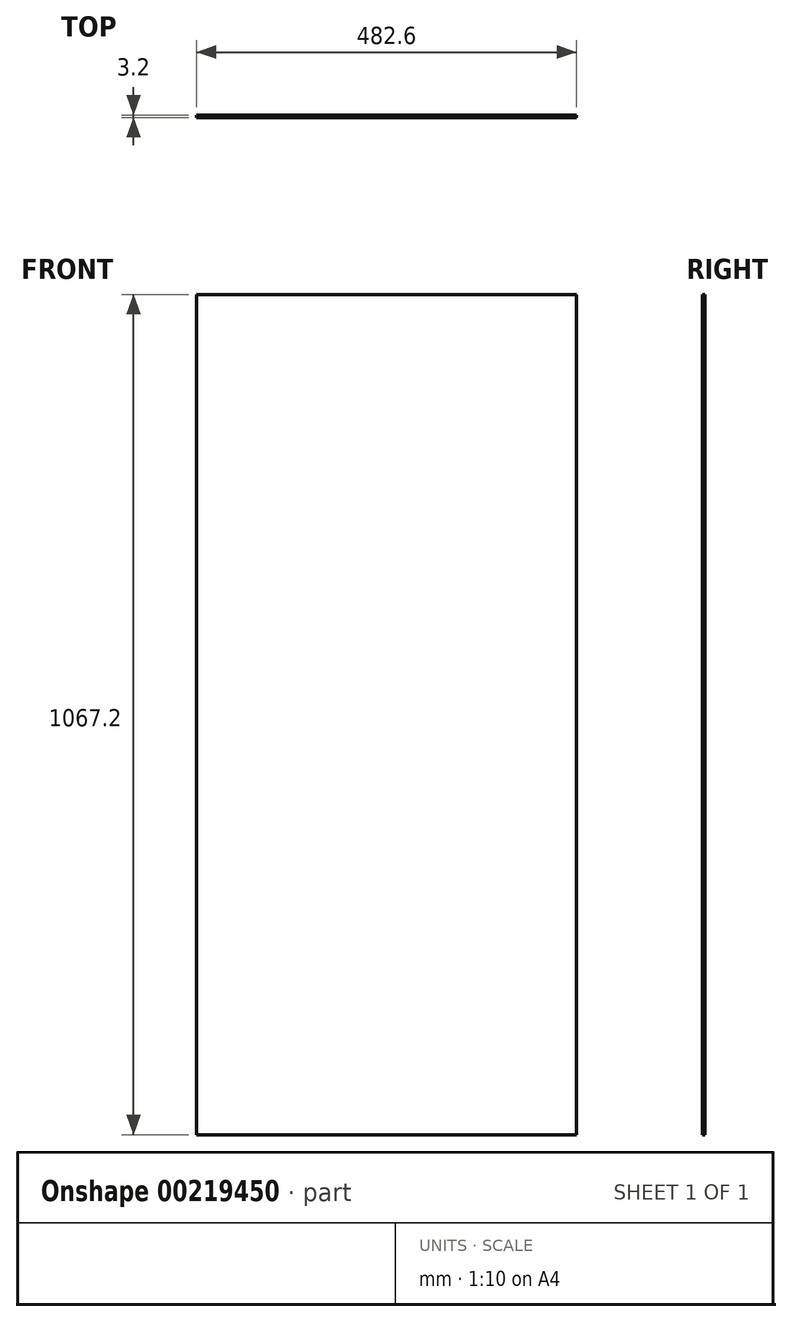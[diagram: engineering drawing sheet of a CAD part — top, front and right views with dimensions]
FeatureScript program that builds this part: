
annotation { "Feature Type Name" : "Feature", "Feature Type Description" : "" }
export const myFeature = defineFeature(function(context is Context, id is Id, definition is map)
    precondition{}
    {
        {
            var Q0;
            Q0=qCreatedBy(makeId("Front.planeOp"),FACE);
            var sketch = newSketch(context, id + "F0", { "sketchPlane" : qUnion([Q0])});
            skLineSegment(sketch, "E0.bottom", {"start": v(-241.3, 533.6) * mm, "end": v(241.3, 533.6) * mm});
            skLineSegment(sketch, "E0.top", {"start": v(-241.3, -533.6) * mm, "end": v(241.3, -533.6) * mm});
            skLineSegment(sketch, "E0.left", {"start": v(-241.3, 533.6) * mm, "end": v(-241.3, -533.6) * mm});
            skLineSegment(sketch, "E0.right", {"start": v(241.3, 533.6) * mm, "end": v(241.3, -533.6) * mm});
            skPoint(sketch, "E0.middle", {"position": v(0, 0) * mm});
            skSolve(sketch);
        }
        {
            var Q0;
            Q0=makeQuery(id+"F0.imprint","IMPRINT",FACE,{"disambiguationData":[TD([[makeQuery(id+"F0.imprint","IMPRINT",EDGE,{"derivedFrom":sQuery(id+"F0.wireOp",EDGE,"E0.bottom")}),-1.0]])]});
            extrude(context, id + "F1", {"entities" : qUnion([Q0]), "oppositeDirection" : true, "depth" : 3.2 * mm});
        }
    });
